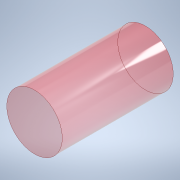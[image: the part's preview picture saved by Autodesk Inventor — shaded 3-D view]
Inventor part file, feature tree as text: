
AUTODESK INVENTOR PART (.ipt)
format: ipt  version: 2020 (Build 240168000, 168)  size: 101,888 bytes
history: native  units: mm
features: extrude x1, sketch x1
ambient origin geometry x8: Origin, YZ Plane, XZ Plane, XY Plane, X Axis, Y Axis, Z Axis, Center Point
bodies: Solid1 (feature_tree)
feature tree (2):
  extrude  "Extrusion1"  Depth=150.0mm TaperAngle=0.0deg
  sketch  "Sketch1"  dims[d0=75.0mm d1=150.0mm d2=0.0mm]
